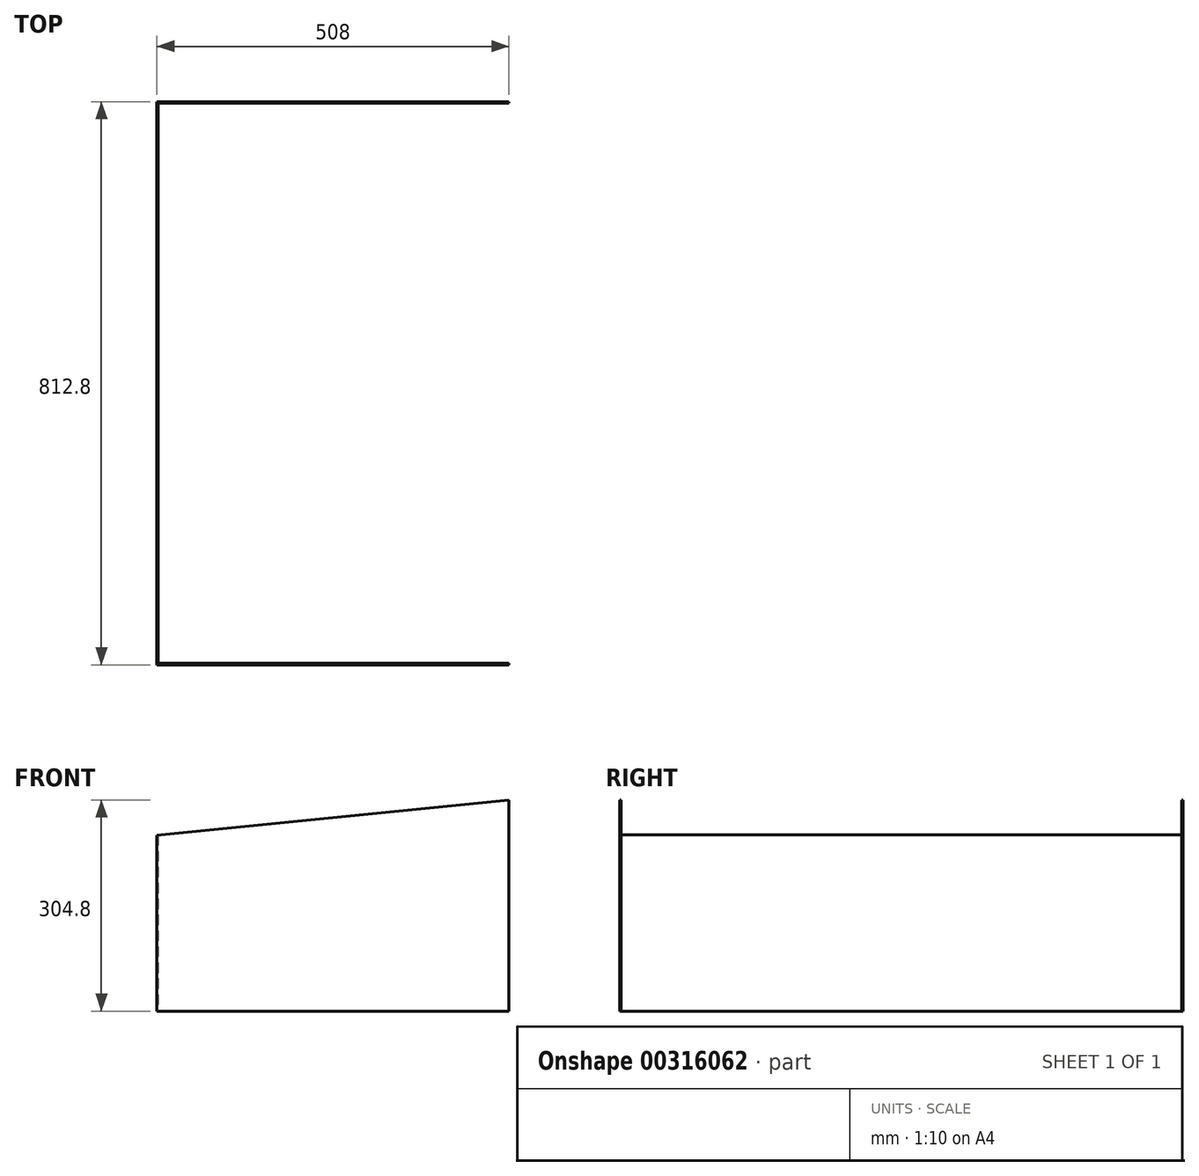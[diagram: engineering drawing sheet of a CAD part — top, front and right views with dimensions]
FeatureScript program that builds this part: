
annotation { "Feature Type Name" : "Feature", "Feature Type Description" : "" }
export const myFeature = defineFeature(function(context is Context, id is Id, definition is map)
    precondition{}
    {
        {
            var Q0;
            Q0=qCreatedBy(makeId("Top.planeOp"),FACE);
            var sketch = newSketch(context, id + "F0", { "sketchPlane" : qUnion([Q0])});
            skLineSegment(sketch, "E0", {"start": v(0, 0) * mm, "end": v(-558.8, 0) * mm});
            skLineSegment(sketch, "E1", {"start": v(-558.8, 0) * mm, "end": v(-558.8, 812.8) * mm});
            skLineSegment(sketch, "E2", {"start": v(-558.8, 812.8) * mm, "end": v(0, 812.8) * mm});
            skLineSegment(sketch, "E3", {"start": v(0, 812.8) * mm, "end": v(0, 810.77) * mm});
            skLineSegment(sketch, "E4", {"start": v(0, 0) * mm, "end": v(0, 2.03) * mm});
            skLineSegment(sketch, "E5", {"start": v(0, 2.03) * mm, "end": v(-556.77, 2.03) * mm});
            skLineSegment(sketch, "E6", {"start": v(-556.77, 2.03) * mm, "end": v(-556.77, 810.77) * mm});
            skLineSegment(sketch, "E7", {"start": v(-556.77, 810.77) * mm, "end": v(0, 810.77) * mm});
            skLineSegment(sketch, "E8.trimOffspring", {"start": v(0, 2.03) * mm, "end": v(0, 0) * mm});
            skSolve(sketch);
        }
        {
            var Q0;
            Q0=makeQuery(id+"F0.imprint","IMPRINT",FACE,{"disambiguationData":[TD([[makeQuery(id+"F0.imprint","IMPRINT",EDGE,{"derivedFrom":sQuery(id+"F0.wireOp",EDGE,"E0")}),-1.0]])]});
            extrude(context, id + "F1", {"entities" : qUnion([Q0]), "depth" : 304.8 * mm});
        }
        {
            var Q0;
            Q0=makeQuery(id+"F1.opExtrude","SWEPT_FACE",FACE,{"disambiguationData":[OSD([sQuery(id+"F0.wireOp",EDGE,"E0")])]});
            var sketch = newSketch(context, id + "F2", { "sketchPlane" : qUnion([Q0])});
            skLineSegment(sketch, "E9", {"start": v(-558.8, 0) * mm, "end": v(-50.8, 0) * mm});
            skLineSegment(sketch, "E10", {"start": v(-50.8, 0) * mm, "end": v(-50.8, 312.96) * mm});
            skLineSegment(sketch, "E11", {"start": v(-50.8, 312.96) * mm, "end": v(22.66, 306.12) * mm});
            skLineSegment(sketch, "E12", {"start": v(22.66, 306.12) * mm, "end": v(29.5, 0) * mm});
            skLineSegment(sketch, "E13", {"start": v(29.5, 0) * mm, "end": v(-50.8, 0) * mm});
            skSolve(sketch);
        }
        {
            var Q0;
            {var subQ3=sQuery(id+"F0.wireOp",EDGE,"E0");var subQ6=makeQuery(id+"F1.opExtrude","SWEPT_EDGE",EDGE,{"disambiguationData":[OSD([subQ3,sQuery(id+"F0.wireOp",EDGE,"E8.trimOffspring")])]});Q0=makeQuery(id+"F2.imprint","IMPRINT",FACE,{"disambiguationData":[TD([[makeQuery(id+"F2.imprint","IMPRINT",EDGE,{"derivedFrom":subQ6}),-1.0]])]});}
            extrude(context, id + "F3", {"entities" : qUnion([Q0]), "operationType" : NewBodyOperationType.REMOVE, "endBound" : BoundingType.THROUGH_ALL, "oppositeDirection" : true, "depth" : 25.4 * mm});
        }
        {
            var Q0;
            Q0=makeQuery(id+"F1.opExtrude","SWEPT_FACE",FACE,{"disambiguationData":[OSD([sQuery(id+"F0.wireOp",EDGE,"E0")])]});
            var sketch = newSketch(context, id + "F4", { "sketchPlane" : qUnion([Q0])});
            skLineSegment(sketch, "E14", {"start": v(-558.8, 0) * mm, "end": v(-558.8, 254) * mm});
            skLineSegment(sketch, "E15", {"start": v(-558.8, 254) * mm, "end": v(-50.8, 304.8) * mm});
            skLineSegment(sketch, "E16", {"start": v(-50.8, 304.8) * mm, "end": v(-532.53, 347.56) * mm});
            skLineSegment(sketch, "E17", {"start": v(-532.53, 347.56) * mm, "end": v(-630.11, 269.49) * mm});
            skLineSegment(sketch, "E18", {"start": v(-630.11, 269.49) * mm, "end": v(-558.8, 254) * mm});
            skSolve(sketch);
        }
        {
            var Q0;
            Q0=makeQuery(id+"F4.imprint","IMPRINT",FACE,{"disambiguationData":[TD([[makeQuery(id+"F4.imprint","IMPRINT",EDGE,{"derivedFrom":sQuery(id+"F4.wireOp",EDGE,"E16")}),1.0]])]});
            var Q1;
            {var subQ0=sQuery(id+"F4.wireOp",EDGE,"E15");Q1=makeQuery(id+"F4.imprint","IMPRINT",FACE,{"disambiguationData":[TD([[makeQuery(id+"F4.imprint","IMPRINT",EDGE,{"derivedFrom":subQ0}),1.0]])]});}
            extrude(context, id + "F5", {"entities" : qUnion([Q0, Q1]), "operationType" : NewBodyOperationType.REMOVE, "endBound" : BoundingType.THROUGH_ALL, "oppositeDirection" : true, "depth" : 25.4 * mm});
        }
    });
